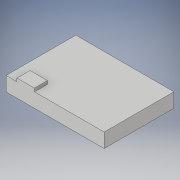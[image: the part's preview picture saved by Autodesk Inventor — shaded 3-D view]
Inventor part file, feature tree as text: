
AUTODESK INVENTOR PART (.ipt)
format: ipt  version: 2018 (Build 220112000, 112)  size: 101,888 bytes
history: native  units: in
note: dims shown in document units (in); Inventor stores cm internally (conversion verified against a paired STEP export)
features: extrude x2, sketch x2
ambient origin geometry x8: Origin, YZ Plane, XZ Plane, XY Plane, X Axis, Y Axis, Z Axis, Center Point
bodies: Solid1 (feature_tree)
feature tree (4):
  extrude  "Extrusion1"  Depth=1.2598in
  extrude  "Extrusion2"  Depth=0.315in
  sketch  "Sketch1"  dims[d0=1.7717in d1=1.2598in]
  sketch  "Sketch2"  dims[d2=0.2579in d3=0.0in d4=0.315in d5=0.2362in d6=0.1969in d7=0.0571in d8=0.0in]
